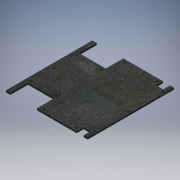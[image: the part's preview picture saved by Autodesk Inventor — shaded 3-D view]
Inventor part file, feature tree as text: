
AUTODESK INVENTOR PART (.ipt)
format: ipt  version: 2019 (Build 230136000, 136)  size: 169,472 bytes
history: native  units: mm
features: sketch x2, other x1, extrude x1, hole x1
ambient origin geometry x8: Origin, YZ Plane, XZ Plane, XY Plane, X Axis, Y Axis, Z Axis, Center Point
bodies: Body1 (feature_tree)
feature tree (5):
  other  "Bryła1"
  extrude  "Wyciągnięcie proste1"  Depth=92.7mm
  hole  "Otwór1"  [1 undecoded]
  sketch  "Szkic1"
  sketch  "Szkic2"
note: 1 required parameter value undecoded (feature->parameter linkage not recoverable at this tier; creation-order binding heuristic only, values carry confidence <= 0.55)
